# Revit family: 1200 Low Storage
name_source: partatom
category: Furniture
units: mm (PartAtom-declared; Revit-internal decimal feet)

## family parameters
Always vertical = Yes
Cut with Voids When Loaded = No
OmniClass Number = 23.40.20.00
OmniClass Title = General Furniture and Specialties
Room Calculation Point = No
Shared = No
Work Plane-Based = No

## types (1)
- Storage - 1200 Low Storage Unit
    Carcass = Gresham - MIDNIGHT ASH VERTICAL
    Depth = 400 mm  [stored 1.31234 ft]
    Doors = Gresham - Azure
    Frame = Gresham - BLACK METAL
    Handle = Gresham - BLACK METAL
    Manufacturer = Gresham Office Furniture
    Model = KULTURE QUOLL
    Product Code = KQ1206ST
    Range = STORAGE
    URL = www.gof.co.uk
    Width = 1200 mm  [stored 3.93701 ft]

note: [stored X ft] marks values corroborated as IEEE doubles in the binary element streams (Revit-internal decimal feet)

## geometry (parser evidence)
native form markers: Sweep x14
no freeform markers — native parametric forms only
